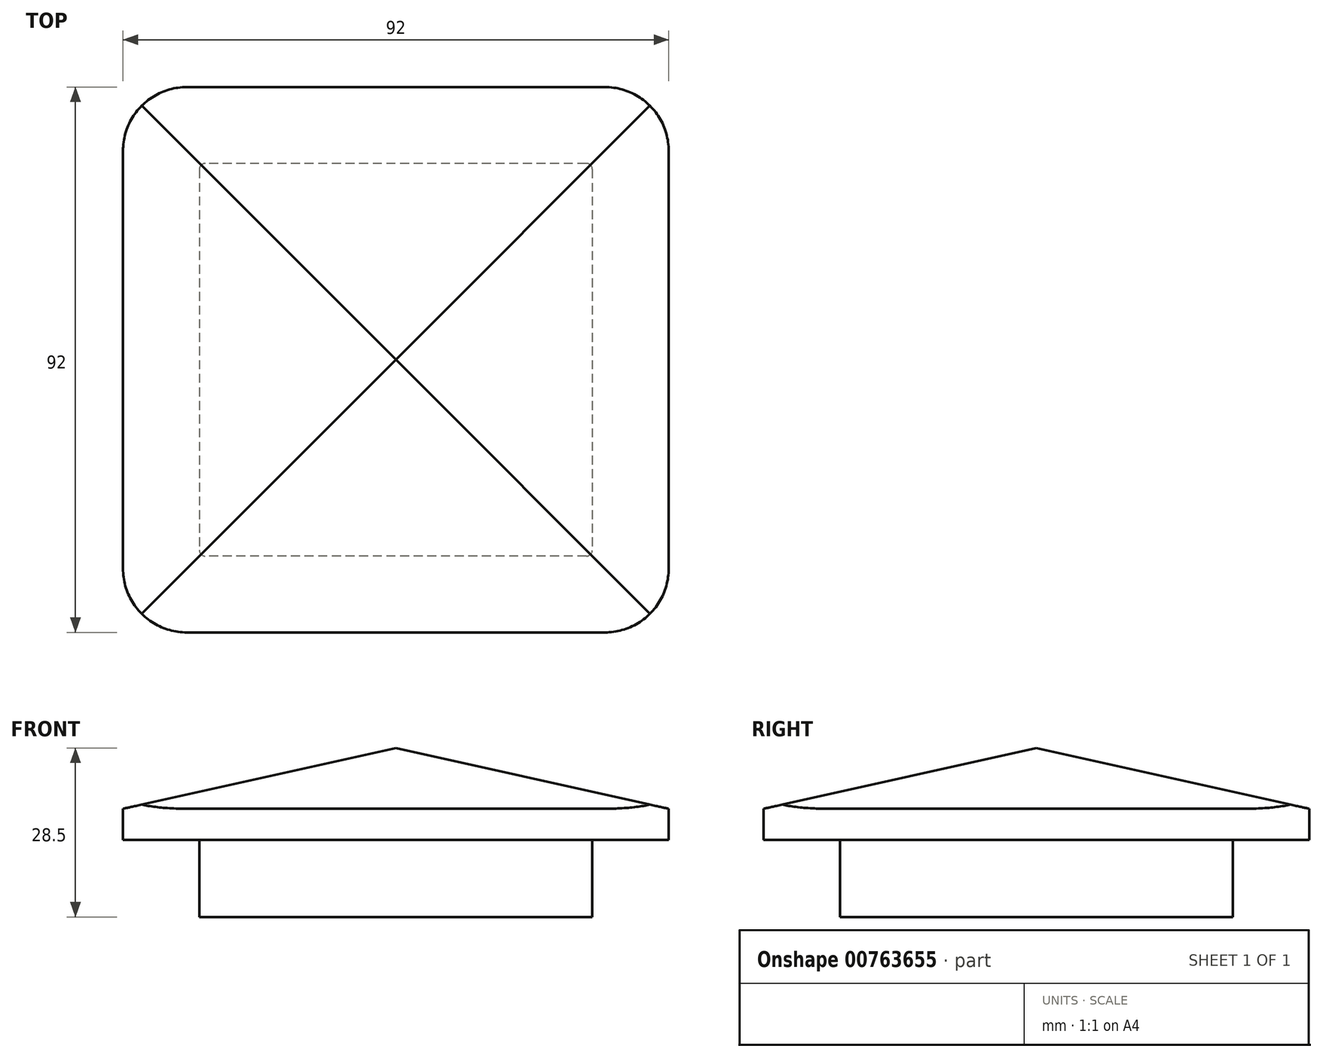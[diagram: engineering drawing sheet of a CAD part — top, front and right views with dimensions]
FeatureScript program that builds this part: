
annotation { "Feature Type Name" : "Feature", "Feature Type Description" : "" }
export const myFeature = defineFeature(function(context is Context, id is Id, definition is map)
    precondition{}
    {
        {
            var Q0;
            Q0=qCreatedBy(makeId("Top.planeOp"),FACE);
            var sketch = newSketch(context, id + "F0", { "sketchPlane" : qUnion([Q0])});
            skLineSegment(sketch, "E0.bottom", {"start": v(-46, 46) * mm, "end": v(46, 46) * mm});
            skLineSegment(sketch, "E0.top", {"start": v(-46, -46) * mm, "end": v(46, -46) * mm});
            skLineSegment(sketch, "E0.left", {"start": v(-46, 46) * mm, "end": v(-46, -46) * mm});
            skLineSegment(sketch, "E0.right", {"start": v(46, 46) * mm, "end": v(46, -46) * mm});
            skSolve(sketch);
        }
        {
            var Q0;
            Q0 = qSketchRegion(id + "F0", true);
            extrude(context, id + "F1", {"entities" : qUnion([Q0]), "depth" : 5.25 * mm, "offsetDistance" : 25 * mm});
        }
        {
            var Q0;
            Q0=makeQuery(id+"F1.opExtrude","CAP_FACE",FACE,{"disambiguationData":[OSD([sQuery(id+"F0.wireOp",EDGE,"E0.bottom"),sQuery(id+"F0.wireOp",EDGE,"E0.top"),sQuery(id+"F0.wireOp",EDGE,"E0.left"),sQuery(id+"F0.wireOp",EDGE,"E0.right")])],"isStart":false});
            cPlane(context, id + "F2", {"entities" : qUnion([Q0]), "cplaneType" : CPlaneType.OFFSET, "offset" : 10.25 * mm, "width" : 150 * mm, "height" : 150 * mm});
        }
        {
            var Q0;
            Q0=qCreatedBy(id+"F2.planeOp",FACE);
            var sketch = newSketch(context, id + "F3", { "sketchPlane" : qUnion([Q0])});
            skPoint(sketch, "E1", {"position": v(0, 0) * mm});
            skSolve(sketch);
        }
        {
            var Q1;
            Q1=makeQuery(id+"F1.opExtrude","CAP_FACE",FACE,{"disambiguationData":[OSD([sQuery(id+"F0.wireOp",EDGE,"E0.bottom"),sQuery(id+"F0.wireOp",EDGE,"E0.top"),sQuery(id+"F0.wireOp",EDGE,"E0.left"),sQuery(id+"F0.wireOp",EDGE,"E0.right")])],"isStart":false});
            var Q2;
            Q2=sQuery(id+"F3.wireOp",VERTEX,"E1");
            loft(context, id + "F4", {"operationType" : NewBodyOperationType.ADD, "sheetProfilesArray" : [{ "sheetProfileEntities" : qUnion([Q1]) }, { "sheetProfileEntities" : qUnion([Q2]) }]});
        }
        {
            var Q0;
            Q0=makeQuery(id+"F1.opExtrude","SWEPT_EDGE",EDGE,{"disambiguationData":[OSD([sQuery(id+"F0.wireOp",EDGE,"E0.top"),sQuery(id+"F0.wireOp",EDGE,"E0.left")])]});
            var Q1;
            Q1=makeQuery(id+"F1.opExtrude","SWEPT_EDGE",EDGE,{"disambiguationData":[OSD([sQuery(id+"F0.wireOp",EDGE,"E0.top"),sQuery(id+"F0.wireOp",EDGE,"E0.right")])]});
            var Q2;
            Q2=makeQuery(id+"F1.opExtrude","SWEPT_EDGE",EDGE,{"disambiguationData":[OSD([sQuery(id+"F0.wireOp",EDGE,"E0.bottom"),sQuery(id+"F0.wireOp",EDGE,"E0.right")])]});
            var Q3;
            Q3=makeQuery(id+"F1.opExtrude","SWEPT_EDGE",EDGE,{"disambiguationData":[OSD([sQuery(id+"F0.wireOp",EDGE,"E0.bottom"),sQuery(id+"F0.wireOp",EDGE,"E0.left")])]});
            fillet(context, id + "F5", {"entities" : qUnion([Q0, Q1, Q2, Q3]), "radius" : 10.75 * mm, "tangentPropagation" : true, "allowEdgeOverflow" : false});
        }
        {
            var Q0;
            Q0=makeQuery(id+"F1.opExtrude","CAP_FACE",FACE,{"disambiguationData":[OSD([sQuery(id+"F0.wireOp",EDGE,"E0.bottom"),sQuery(id+"F0.wireOp",EDGE,"E0.top"),sQuery(id+"F0.wireOp",EDGE,"E0.left"),sQuery(id+"F0.wireOp",EDGE,"E0.right")])],"isStart":true});
            var sketch = newSketch(context, id + "F6", { "sketchPlane" : qUnion([Q0])});
            skLineSegment(sketch, "E2.bottom", {"start": v(33.12, -33.12) * mm, "end": v(-33.12, -33.13) * mm});
            skLineSegment(sketch, "E2.top", {"start": v(33.12, 33.13) * mm, "end": v(-33.13, 33.12) * mm});
            skLineSegment(sketch, "E2.left", {"start": v(33.12, -33.12) * mm, "end": v(33.12, 33.12) * mm});
            skLineSegment(sketch, "E2.right", {"start": v(-33.12, -33.12) * mm, "end": v(-33.13, 33.12) * mm});
            skSolve(sketch);
        }
        {
            var Q0;
            Q0 = qSketchRegion(id + "F6", true);
            extrude(context, id + "F7", {"entities" : qUnion([Q0]), "operationType" : NewBodyOperationType.ADD, "depth" : 13 * mm, "offsetDistance" : 25 * mm});
        }
        {
            var Q0;
            Q0=makeQuery(id+"F7.opExtrude","SWEPT_EDGE",EDGE,{"disambiguationData":[OSD([sQuery(id+"F6.wireOp",EDGE,"E2.bottom"),sQuery(id+"F6.wireOp",EDGE,"E2.left")])]});
            var Q1;
            Q1=makeQuery(id+"F7.opExtrude","SWEPT_EDGE",EDGE,{"disambiguationData":[OSD([sQuery(id+"F6.wireOp",EDGE,"E2.bottom"),sQuery(id+"F6.wireOp",EDGE,"E2.right")])]});
            var Q2;
            Q2=makeQuery(id+"F7.opExtrude","SWEPT_EDGE",EDGE,{"disambiguationData":[OSD([sQuery(id+"F6.wireOp",EDGE,"E2.top"),sQuery(id+"F6.wireOp",EDGE,"E2.right")])]});
            var Q3;
            Q3=makeQuery(id+"F7.opExtrude","SWEPT_EDGE",EDGE,{"disambiguationData":[OSD([sQuery(id+"F6.wireOp",EDGE,"E2.top"),sQuery(id+"F6.wireOp",EDGE,"E2.left")])]});
            fillet(context, id + "F8", {"entities" : qUnion([Q0, Q1, Q2, Q3]), "radius" : 1 * mm, "tangentPropagation" : true, "allowEdgeOverflow" : false});
        }
    });
